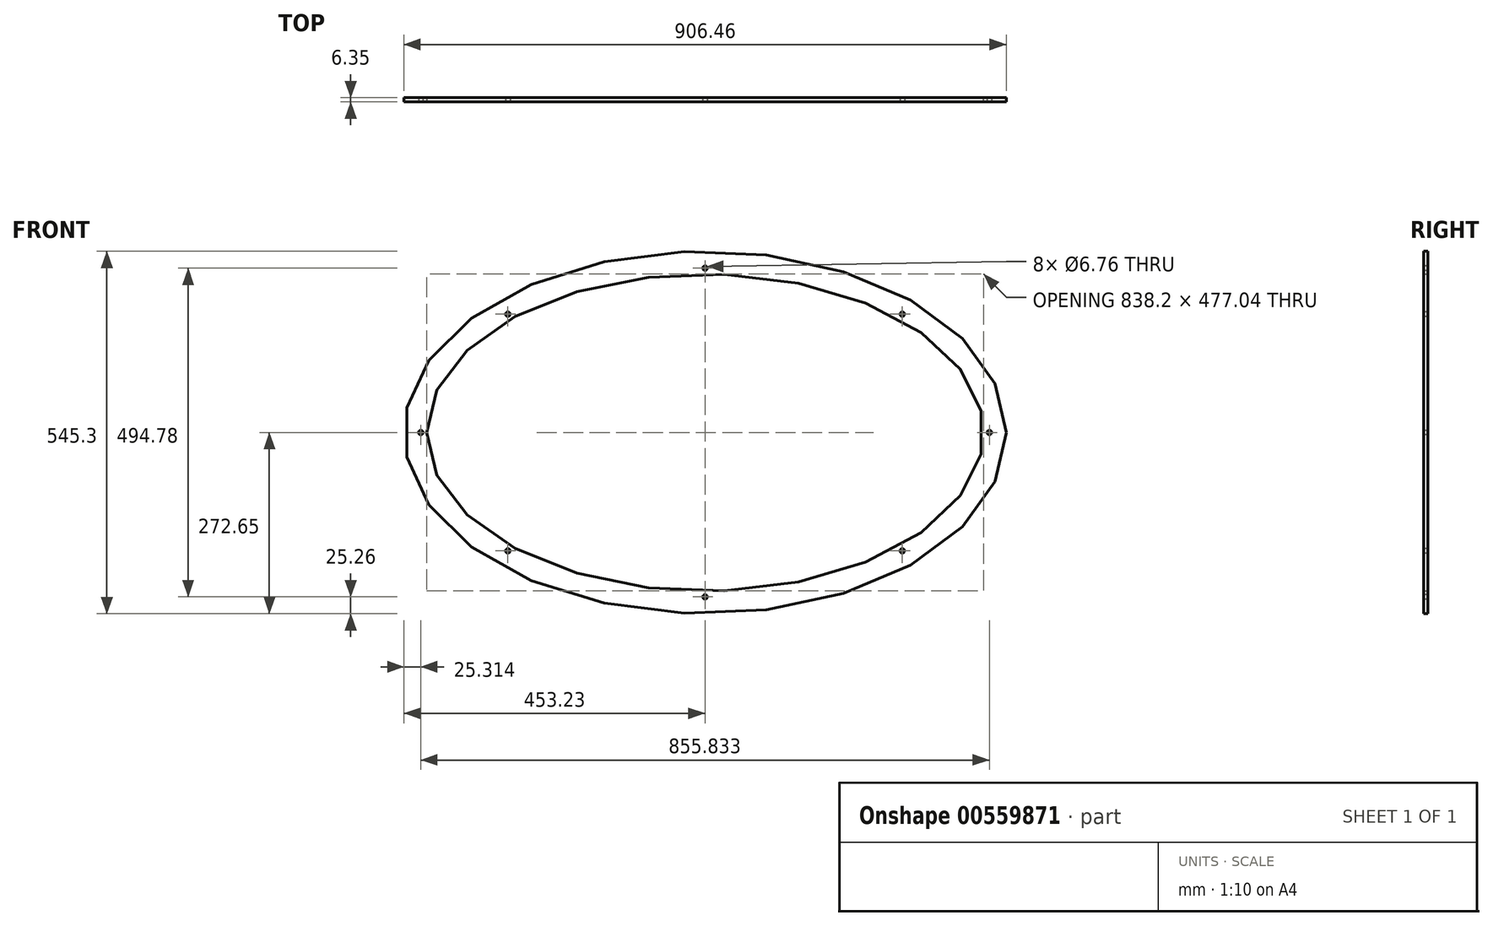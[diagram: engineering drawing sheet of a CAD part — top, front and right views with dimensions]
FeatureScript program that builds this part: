
annotation { "Feature Type Name" : "Feature", "Feature Type Description" : "" }
export const myFeature = defineFeature(function(context is Context, id is Id, definition is map)
    precondition{}
    {
        {
            var Q0;
            Q0=qCreatedBy(makeId("Front.planeOp"),FACE);
            var sketch = newSketch(context, id + "F0", { "sketchPlane" : qUnion([Q0])});
            skEllipse(sketch, "E0", {"center": v(0, 0) * mm, "majorRadius": 453.23 * mm, "minorRadius": 272.65 * mm, "majorAxis": v(1, 0)});
            skSolve(sketch);
        }
        {
            var Q0;
            Q0=makeQuery(id+"F0.imprint","IMPRINT",FACE,{"disambiguationData":[TD([[makeQuery(id+"F0.imprint","IMPRINT",EDGE,{"derivedFrom":sQuery(id+"F0.wireOp",EDGE,"E0")}),1.0]])]});
            extrude(context, id + "F1", {"entities" : qUnion([Q0]), "depth" : 6.35 * mm, "offsetDistance" : 25.4 * mm});
        }
        {
            var Q0;
            Q0=makeQuery(id+"F1.opExtrude","CAP_FACE",FACE,{"disambiguationData":[OSD([sQuery(id+"F0.wireOp",EDGE,"E0")])],"isStart":false});
            var sketch = newSketch(context, id + "F2", { "sketchPlane" : qUnion([Q0])});
            skPoint(sketch, "E1", {"position": v(0, 247.4) * mm});
            skPoint(sketch, "E2", {"position": v(-427.92, 0) * mm});
            skPoint(sketch, "E3", {"position": v(-296.82, 178.08) * mm});
            skPoint(sketch, "E4", {"position": v(-296.82, -178.13) * mm});
            skPoint(sketch, "E5.MirrorP", {"position": v(296.82, -178.13) * mm});
            skPoint(sketch, "E6.MirrorP", {"position": v(296.82, 178.08) * mm});
            skPoint(sketch, "E7.MirrorP", {"position": v(427.92, 0) * mm});
            skPoint(sketch, "E8.MirrorP", {"position": v(0, -247.4) * mm});
            skSolve(sketch);
        }
        {
            var Q0;
            Q0=sQuery(id+"F2.wireOp",VERTEX,"E2");
            var Q1;
            Q1=sQuery(id+"F2.wireOp",VERTEX,"E3");
            var Q2;
            Q2=sQuery(id+"F2.wireOp",VERTEX,"E1");
            var Q3;
            Q3=sQuery(id+"F2.wireOp",VERTEX,"E6.MirrorP");
            var Q4;
            Q4=sQuery(id+"F2.wireOp",VERTEX,"E7.MirrorP");
            var Q5;
            Q5=sQuery(id+"F2.wireOp",VERTEX,"E5.MirrorP");
            var Q6;
            Q6=sQuery(id+"F2.wireOp",VERTEX,"E8.MirrorP");
            var Q7;
            Q7=sQuery(id+"F2.wireOp",VERTEX,"E4");
            var Q8;
            Q8=makeQuery(id+"F1.opExtrude","SWEPT_BODY",BODY,{"disambiguationData":[OSD([sQuery(id+"F0.wireOp",EDGE,"E0")])]});
            hole(context, id + "F3", {"style" : HoleStyle.SIMPLE, "endStyle" : HoleEndStyle.THROUGH, "holeDiameter" : 6.76 * mm, "isTappedThrough" : true, "tappedDepth" : 12.7 * mm, "tapClearance" : 3, "startFromSketch" : true, "locations" : qUnion([Q0, Q1, Q2, Q3, Q4, Q5, Q6, Q7]), "scope" : qUnion([Q8])});
        }
        {
            var Q0;
            Q0=makeQuery(id+"F2.imprint","IMPRINT",FACE,{"disambiguationData":[TD([[makeQuery(id+"F2.imprint","IMPRINT",EDGE,{"derivedFrom":makeQuery(id+"F1.opExtrude","CAP_EDGE",EDGE,{"disambiguationData":[OSD([sQuery(id+"F0.wireOp",EDGE,"E0")])],"isStart":false})}),1.0]])]});
            var sketch = newSketch(context, id + "F4", { "sketchPlane" : qUnion([Q0])});
            skEllipse(sketch, "E9", {"center": v(0, 0) * mm, "majorRadius": 419.1 * mm, "minorRadius": 238.52 * mm, "majorAxis": v(-1, 0)});
            skSolve(sketch);
        }
        {
            var Q0;
            Q0 = qSketchRegion(id + "F4", true);
            var Q1;
            Q1=sQuery(id+"F4.wireOp",EDGE,"E9");
            extrude(context, id + "F5", {"entities" : qUnion([Q0]), "operationType" : NewBodyOperationType.REMOVE, "surfaceEntities" : qUnion([Q1]), "endBound" : BoundingType.THROUGH_ALL, "oppositeDirection" : true, "depth" : 6.35 * mm, "offsetDistance" : 25.4 * mm});
        }
    });
